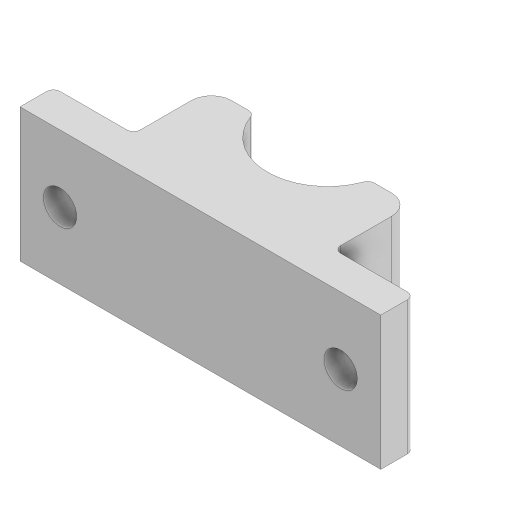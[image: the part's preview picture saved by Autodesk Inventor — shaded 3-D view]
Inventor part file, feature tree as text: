
AUTODESK INVENTOR PART (.ipt)
format: ipt  version: 2023 (Build 270158000, 158)  size: 139,776 bytes
history: native  units: mm
features: fillet x4, sketch x3, extrude x2, mirror x1
ambient origin geometry x8: Origin, YZ Plane, XZ Plane, XY Plane, X Axis, Y Axis, Z Axis, Center Point
bodies: Solid1 (feature_tree)
feature tree (10):
  extrude  "Extrusion1"  Depth=19.05mm
  extrude  "Extrusion2"  Depth=10.0mm
  mirror  "Mirror1"
  fillet  "Fillet2"  Radius=27.0mm
  fillet  "Fillet3"  Radius=20.0mm
  sketch  "Sketch3"  dims[d12=5.0mm d13=5.0mm d14=0.0mm d15=0.0mm d17=1.0mm d18=1.0mm d19=1.0mm d20=3.0mm]
  fillet  "Fillet4"  Radius=6.0mm
  fillet  "Fillet5"  Radius=10.0mm
  sketch  "Sketch1"  dims[d0=18.0mm d1=19.05mm]
  sketch  "Sketch2"  dims[d5=15.0mm d6=15.0mm d7=27.0mm d8=20.0mm d9=0.0mm d10=6.0mm d11=10.0mm]
